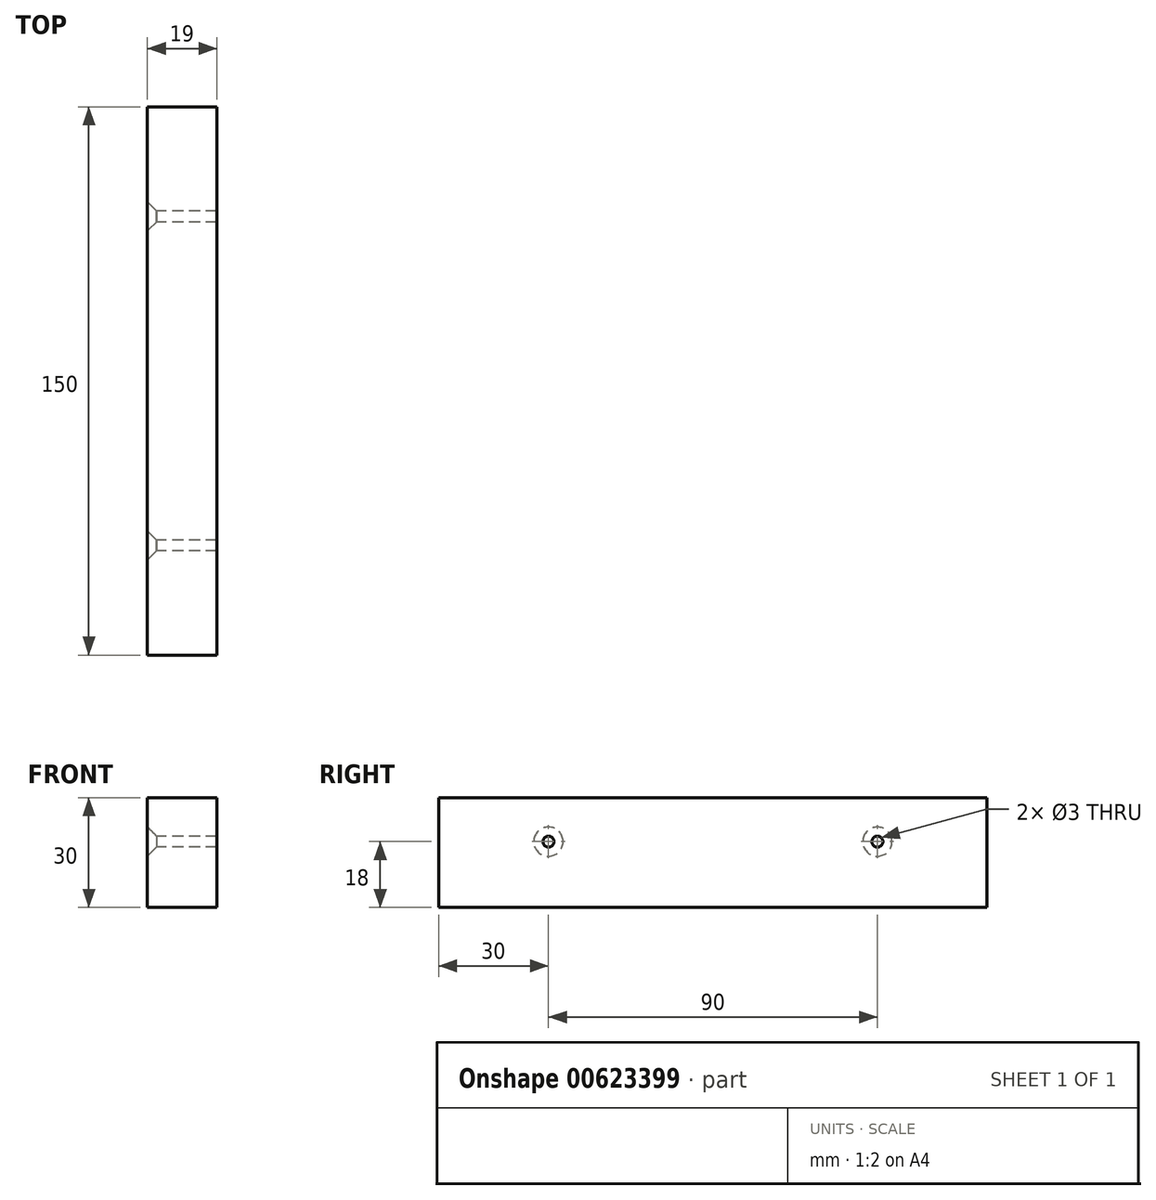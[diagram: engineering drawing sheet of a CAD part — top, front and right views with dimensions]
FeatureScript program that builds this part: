
annotation { "Feature Type Name" : "Feature", "Feature Type Description" : "" }
export const myFeature = defineFeature(function(context is Context, id is Id, definition is map)
    precondition{}
    {
        {
            var Q0;
            Q0=qCreatedBy(makeId("Top.planeOp"),FACE);
            var sketch = newSketch(context, id + "F0", { "sketchPlane" : qUnion([Q0])});
            skLineSegment(sketch, "E0", {"start": v(-50, 0) * mm, "end": v(50, 0) * mm, "construction": true});
            skLineSegment(sketch, "E1", {"start": v(0, 50) * mm, "end": v(0, -50) * mm, "construction": true});
            skSolve(sketch);
        }
        {
            var Q0;
            Q0=qCreatedBy(makeId("Right.planeOp"),FACE);
            var sketch = newSketch(context, id + "F1", { "sketchPlane" : qUnion([Q0])});
            skLineSegment(sketch, "E2", {"start": v(0, 50) * mm, "end": v(0, -50) * mm, "construction": true});
            skSolve(sketch);
        }
        {
            var Q0;
            Q0=qCreatedBy(makeId("Front.planeOp"),FACE);
            var sketch = newSketch(context, id + "F2", { "sketchPlane" : qUnion([Q0])});
            skLineSegment(sketch, "E3.bottom", {"start": v(0, -15) * mm, "end": v(19, -15) * mm});
            skLineSegment(sketch, "E3.top", {"start": v(0, 15) * mm, "end": v(19, 15) * mm});
            skLineSegment(sketch, "E3.left", {"start": v(0, -15) * mm, "end": v(0, 15) * mm});
            skLineSegment(sketch, "E3.right", {"start": v(19, -15) * mm, "end": v(19, 15) * mm});
            skSolve(sketch);
        }
        {
            var Q0;
            Q0=makeQuery(id+"F2.imprint","IMPRINT",FACE,{"disambiguationData":[TD([[makeQuery(id+"F2.imprint","IMPRINT",EDGE,{"derivedFrom":sQuery(id+"F2.wireOp",EDGE,"E3.bottom")}),1.0]])]});
            var Q1;
            Q1=qConstructionFilter(qBodyType(qCreatedBy(id+"F2",EDGE),BodyType.WIRE),ConstructionObject.NO);
            extrude(context, id + "F3", {"entities" : qUnion([Q0]), "surfaceEntities" : qUnion([Q1]), "endBound" : BoundingType.SYMMETRIC, "depth" : 150 * mm, "offsetDistance" : 25 * mm});
        }
        {
            var Q0;
            Q0=makeQuery(id+"F3.opExtrude","SWEPT_FACE",FACE,{"disambiguationData":[OSD([sQuery(id+"F2.wireOp",EDGE,"E3.left")])]});
            var sketch = newSketch(context, id + "F4", { "sketchPlane" : qUnion([Q0])});
            skPoint(sketch, "E4", {"position": v(-45, 3) * mm});
            skPoint(sketch, "E5", {"position": v(45, 3) * mm});
            skSolve(sketch);
        }
        {
            var Q0;
            Q0=sQuery(id+"F4.wireOp",VERTEX,"E4");
            var Q1;
            Q1=sQuery(id+"F4.wireOp",VERTEX,"E5");
            var Q2;
            Q2=makeQuery(id+"F3.opExtrude","SWEPT_BODY",BODY,{"disambiguationData":[OSD([sQuery(id+"F2.wireOp",EDGE,"E3.bottom"),sQuery(id+"F2.wireOp",EDGE,"E3.top"),sQuery(id+"F2.wireOp",EDGE,"E3.left"),sQuery(id+"F2.wireOp",EDGE,"E3.right")])]});
            hole(context, id + "F5", {"style" : HoleStyle.C_SINK, "endStyle" : HoleEndStyle.THROUGH, "holeDiameter" : 3 * mm, "cSinkDiameter" : 8 * mm, "cSinkAngle" : 90 * degree, "majorDiameter" : 5 * mm, "isTappedThrough" : true, "tappedDepth" : 12 * mm, "tapClearance" : 3, "startFromSketch" : true, "locations" : qUnion([Q0, Q1]), "scope" : qUnion([Q2])});
        }
    });
